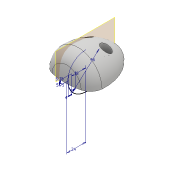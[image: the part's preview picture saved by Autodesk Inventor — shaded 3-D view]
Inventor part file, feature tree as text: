
AUTODESK INVENTOR PART (.ipt)
format: ipt  version: 2017 (Build 210142000, 142)  size: 195,072 bytes
history: native  units: mm
features: sketch x6, extrude x5, fillet x2, revolve x1, thicken_offset x1, plane x1
ambient origin geometry x8: Origin, YZ Plane, XZ Plane, XY Plane, X Axis, Y Axis, Z Axis, Center Point
bodies: Solid1 (feature_tree)
feature tree (16):
  revolve  "Revolution1"  [1 undecoded]
  fillet  "Fillet1"  Radius=80.0mm
  fillet  "Fillet2"  Radius=4.0mm
  thicken_offset  "Thicken1"
  extrude  "Extrusion1"  Depth=20.0mm
  extrude  "Extrusion2"  Depth=4.0mm
  sketch  "Sketch4"  dims[d8=4.0mm d9=10.0mm d10=0.0mm]
  extrude  "Extrusion3"  Depth=10.0mm TaperAngle=0.0deg
  sketch  "Sketch5"  dims[d11=40.0mm d12=12.0mm]
  extrude  "Extrusion4"  Depth=12.0mm
  plane  "Work Plane1"
  extrude  "Extrusion5"  Depth=5.0mm
  sketch  "Sketch1"  dims[d0=32.0mm d1=32.0mm d2=80.0mm d3=4.0mm]
  sketch  "Sketch2"  dims[d4=90.0deg d5=20.0mm]
  sketch  "Sketch3"  dims[d6=20.0mm d7=4.0mm]
  sketch  "Sketch6"  dims[d13=12.0mm d14=12.0mm d15=12.0mm d16=10.0mm d17=0.0mm d18=46.0mm d19=24.0mm d20=38.0mm d21=0.0mm d22=5.75mm d23=18.0mm d24=4.0mm d25=5.0mm d26=5.75mm d27=36.0mm d28=0.0mm d29=-8.0mm d30=20.5mm d31=0.0mm]
note: 1 required parameter value undecoded (feature->parameter linkage not recoverable at this tier; creation-order binding heuristic only, values carry confidence <= 0.55)
